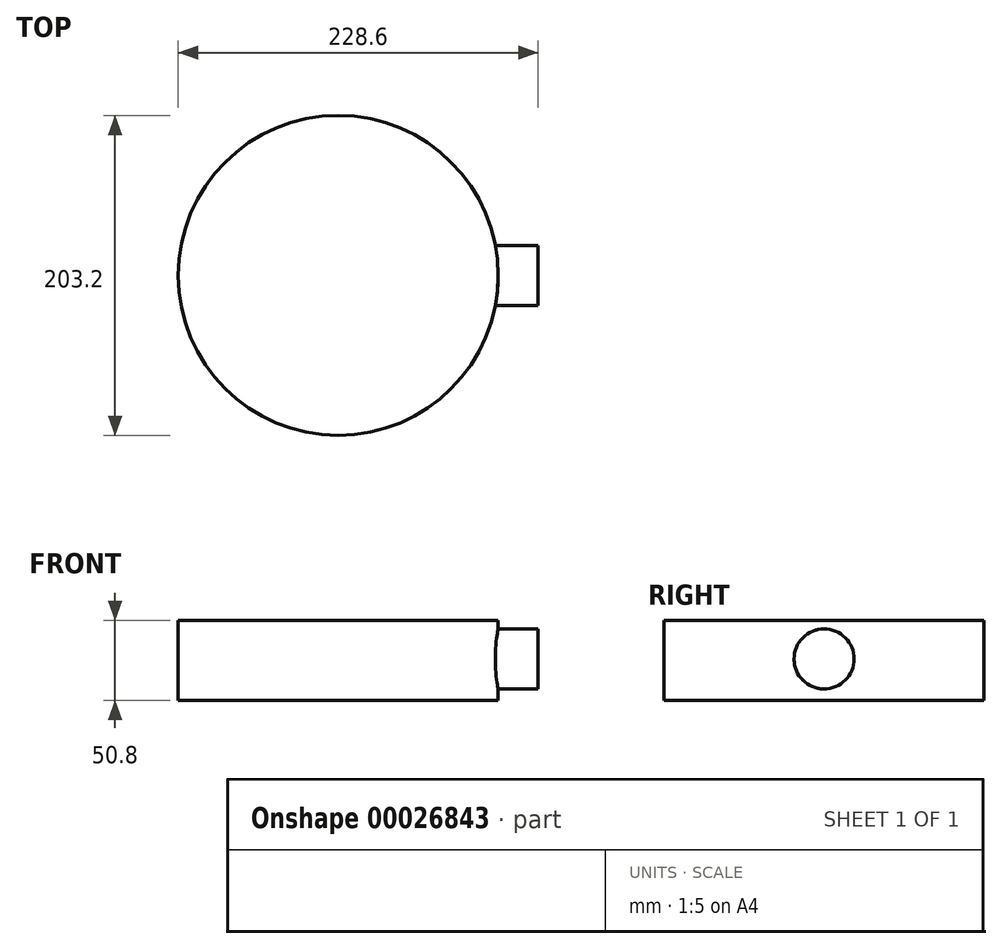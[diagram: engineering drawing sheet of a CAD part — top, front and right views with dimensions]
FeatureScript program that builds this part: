
annotation { "Feature Type Name" : "Feature", "Feature Type Description" : "" }
export const myFeature = defineFeature(function(context is Context, id is Id, definition is map)
    precondition{}
    {
        {
            var Q0;
            Q0=qCreatedBy(makeId("Front.planeOp"),FACE);
            var sketch = newSketch(context, id + "F0", { "sketchPlane" : qUnion([Q0])});
            skLineSegment(sketch, "E0.bottom", {"start": v(-101.6, 27) * mm, "end": v(0, 27) * mm});
            skLineSegment(sketch, "E0.top", {"start": v(-101.6, -23.8) * mm, "end": v(0, -23.8) * mm});
            skLineSegment(sketch, "E0.left", {"start": v(-101.6, 27) * mm, "end": v(-101.6, -23.8) * mm});
            skLineSegment(sketch, "E0.right", {"start": v(0, 27) * mm, "end": v(0, -23.8) * mm});
            skSolve(sketch);
        }
        {
            var Q0;
            Q0=makeQuery(id+"F0.imprint","IMPRINT",FACE,{"disambiguationData":[TD([[makeQuery(id+"F0.imprint","IMPRINT",EDGE,{"derivedFrom":sQuery(id+"F0.wireOp",EDGE,"E0.bottom")}),-1.0]])]});
            var Q1;
            Q1=sQuery(id+"F0.wireOp",EDGE,"E0.right");
            revolve(context, id + "F1", {"entities" : qUnion([Q0]), "axis" : qUnion([Q1]), "revolveType" : RevolveType.FULL});
        }
        {
            var Q0;
            Q0=qCreatedBy(makeId("Right.planeOp"),FACE);
            var sketch = newSketch(context, id + "F2", { "sketchPlane" : qUnion([Q0])});
            skCircle(sketch, "E1", {"center": v(0, 2.5) * mm, "radius": 19.05 * mm});
            skSolve(sketch);
        }
        {
            var Q0;
            Q0 = qSketchRegion(id + "F2", true);
            extrude(context, id + "F3", {"entities" : qUnion([Q0]), "operationType" : NewBodyOperationType.ADD, "depth" : 127 * mm});
        }
    });
